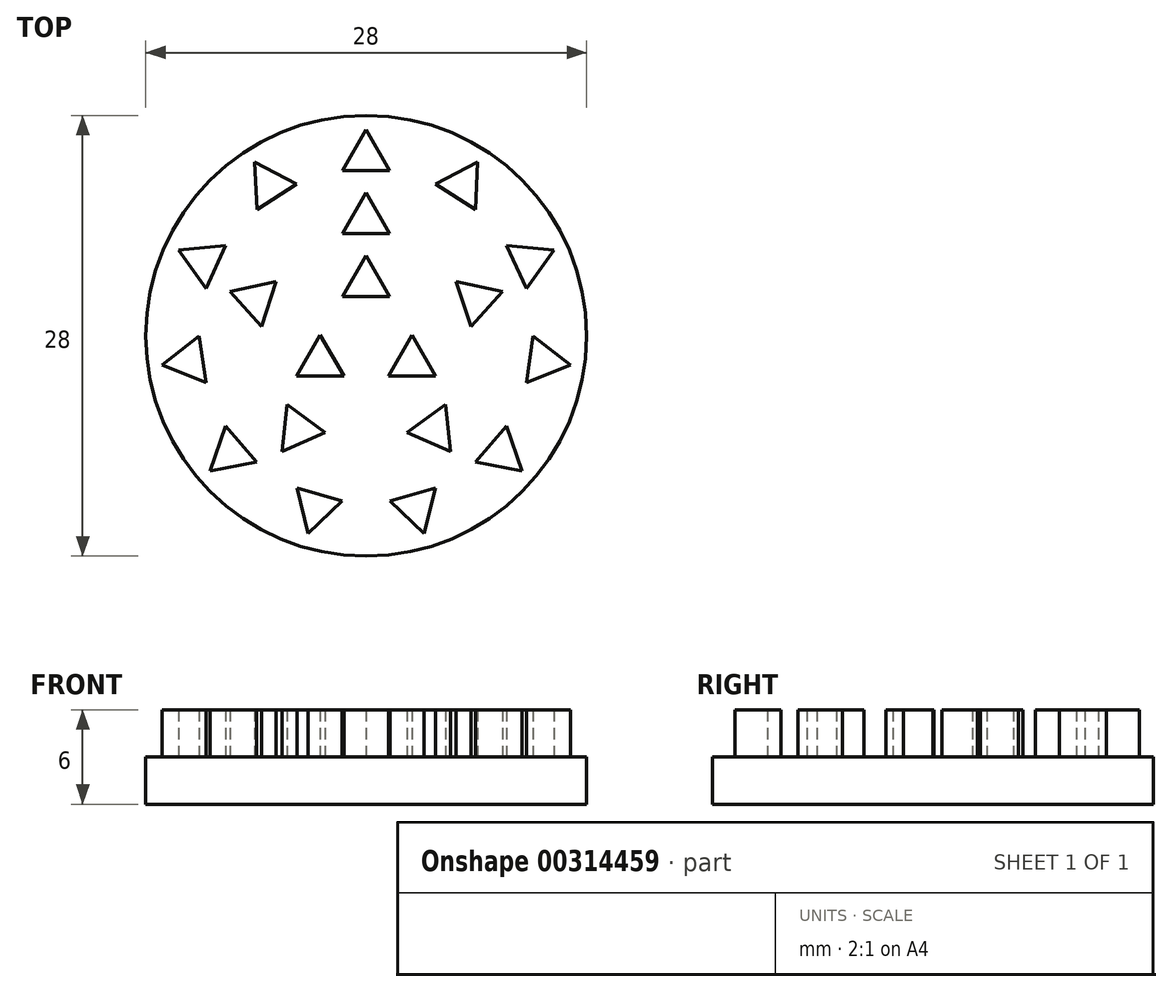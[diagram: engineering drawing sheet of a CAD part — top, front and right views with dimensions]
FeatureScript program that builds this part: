
annotation { "Feature Type Name" : "Feature", "Feature Type Description" : "" }
export const myFeature = defineFeature(function(context is Context, id is Id, definition is map)
    precondition{}
    {
        {
            var Q0;
            Q0=qCreatedBy(makeId("Top.planeOp"),FACE);
            var sketch = newSketch(context, id + "F0", { "sketchPlane" : qUnion([Q0])});
            skCircle(sketch, "E0", {"center": v(0, 0) * mm, "radius": 14 * mm});
            skSolve(sketch);
        }
        {
            var Q0;
            Q0=makeQuery(id+"F0.imprint","IMPRINT",FACE,{"disambiguationData":[TD([[makeQuery(id+"F0.imprint","IMPRINT",EDGE,{"derivedFrom":sQuery(id+"F0.wireOp",EDGE,"E0")}),1.0]])]});
            extrude(context, id + "F1", {"entities" : qUnion([Q0]), "depth" : 3 * mm});
        }
        {
            var Q0;
            Q0=makeQuery(id+"F1.opExtrude","CAP_FACE",FACE,{"disambiguationData":[OSD([sQuery(id+"F0.wireOp",EDGE,"E0")])],"isStart":false});
            var sketch = newSketch(context, id + "F2", { "sketchPlane" : qUnion([Q0])});
            skCircle(sketch, "E1.cCircle", {"center": v(0, 7.37) * mm, "radius": 0.87 * mm, "construction": true});
            skLineSegment(sketch, "E1.0", {"start": v(1.5, 6.5) * mm, "end": v(-1.5, 6.5) * mm});
            skLineSegment(sketch, "E1.1", {"start": v(-1.5, 6.5) * mm, "end": v(0, 9.1) * mm});
            skLineSegment(sketch, "E1.2", {"start": v(0, 9.1) * mm, "end": v(1.5, 6.5) * mm});
            skPoint(sketch, "E1.0.midPoint", {"position": v(0, 6.5) * mm});
            skCircle(sketch, "E2", {"center": v(0, 0) * mm, "radius": 6.5 * mm});
            skLineSegment(sketch, "E3.1.0", {"start": v(-5.72, 3.44) * mm, "end": v(-6.65, 0.58) * mm});
            skLineSegment(sketch, "E3.1.1", {"start": v(-8.65, 2.81) * mm, "end": v(-5.72, 3.44) * mm});
            skLineSegment(sketch, "E3.1.2", {"start": v(-6.65, 0.58) * mm, "end": v(-8.65, 2.81) * mm});
            skCircle(sketch, "E3.1.3", {"center": v(-7, 2.28) * mm, "radius": 0.87 * mm, "construction": true});
            skLineSegment(sketch, "E3.2.0", {"start": v(-5.03, -4.38) * mm, "end": v(-2.6, -6.14) * mm});
            skLineSegment(sketch, "E3.2.1", {"start": v(-5.35, -7.36) * mm, "end": v(-5.03, -4.38) * mm});
            skLineSegment(sketch, "E3.2.2", {"start": v(-2.6, -6.14) * mm, "end": v(-5.35, -7.36) * mm});
            skCircle(sketch, "E3.2.3", {"center": v(-4.33, -5.96) * mm, "radius": 0.87 * mm, "construction": true});
            skCircle(sketch, "E4.cCircle", {"center": v(0, 11.37) * mm, "radius": 0.87 * mm, "construction": true});
            skLineSegment(sketch, "E4.0", {"start": v(1.5, 10.5) * mm, "end": v(-1.5, 10.5) * mm});
            skLineSegment(sketch, "E4.1", {"start": v(-1.5, 10.5) * mm, "end": v(0, 13.1) * mm});
            skLineSegment(sketch, "E4.2", {"start": v(0, 13.1) * mm, "end": v(1.5, 10.5) * mm});
            skPoint(sketch, "E4.0.midPoint", {"position": v(0, 10.5) * mm});
            skCircle(sketch, "E5", {"center": v(0, 0) * mm, "radius": 10.5 * mm});
            skLineSegment(sketch, "E6.1.0", {"start": v(-4.41, 9.64) * mm, "end": v(-6.94, 8.02) * mm});
            skLineSegment(sketch, "E6.1.1", {"start": v(-7.08, 11.02) * mm, "end": v(-4.41, 9.64) * mm});
            skLineSegment(sketch, "E6.1.2", {"start": v(-6.94, 8.02) * mm, "end": v(-7.08, 11.02) * mm});
            skCircle(sketch, "E6.1.3", {"center": v(-6.14, 9.56) * mm, "radius": 0.87 * mm, "construction": true});
            skLineSegment(sketch, "E6.2.0", {"start": v(-8.93, 5.73) * mm, "end": v(-10.17, 3) * mm});
            skLineSegment(sketch, "E6.2.1", {"start": v(-11.91, 5.44) * mm, "end": v(-8.93, 5.73) * mm});
            skLineSegment(sketch, "E6.2.2", {"start": v(-10.17, 3) * mm, "end": v(-11.91, 5.44) * mm});
            skCircle(sketch, "E6.2.3", {"center": v(-10.34, 4.72) * mm, "radius": 0.87 * mm, "construction": true});
            skLineSegment(sketch, "E7.2.3.0", {"start": v(-10.6, 0) * mm, "end": v(-10.18, -2.98) * mm});
            skLineSegment(sketch, "E7.3.3.0", {"start": v(-12.96, -1.86) * mm, "end": v(-10.6, 0) * mm});
            skLineSegment(sketch, "E7.6.3.0", {"start": v(-10.18, -2.98) * mm, "end": v(-12.96, -1.86) * mm});
            skCircle(sketch, "E7.9.3.0", {"center": v(-11.25, -1.62) * mm, "radius": 0.87 * mm, "construction": true});
            skLineSegment(sketch, "E7.2.4.0", {"start": v(-8.92, -5.74) * mm, "end": v(-6.95, -8) * mm});
            skLineSegment(sketch, "E7.3.4.0", {"start": v(-9.9, -8.58) * mm, "end": v(-8.92, -5.74) * mm});
            skLineSegment(sketch, "E7.6.4.0", {"start": v(-6.95, -8) * mm, "end": v(-9.9, -8.58) * mm});
            skCircle(sketch, "E7.9.4.0", {"center": v(-8.59, -7.44) * mm, "radius": 0.87 * mm, "construction": true});
            skLineSegment(sketch, "E7.2.5.0", {"start": v(-4.4, -9.65) * mm, "end": v(-1.52, -10.5) * mm});
            skLineSegment(sketch, "E7.3.5.0", {"start": v(-3.7, -12.57) * mm, "end": v(-4.4, -9.65) * mm});
            skLineSegment(sketch, "E7.6.5.0", {"start": v(-1.52, -10.5) * mm, "end": v(-3.7, -12.57) * mm});
            skCircle(sketch, "E7.9.5.0", {"center": v(-3.2, -10.9) * mm, "radius": 0.87 * mm, "construction": true});
            skLineSegment(sketch, "E7.2.6.0", {"start": v(1.52, -10.5) * mm, "end": v(4.4, -9.65) * mm});
            skLineSegment(sketch, "E7.3.6.0", {"start": v(3.7, -12.57) * mm, "end": v(1.52, -10.5) * mm});
            skLineSegment(sketch, "E7.6.6.0", {"start": v(4.4, -9.65) * mm, "end": v(3.7, -12.57) * mm});
            skCircle(sketch, "E7.9.6.0", {"center": v(3.2, -10.9) * mm, "radius": 0.87 * mm, "construction": true});
            skPoint(sketch, "E8", {"position": v(5.68, 8.83) * mm});
            skPoint(sketch, "E9", {"position": v(-2.96, -10.07) * mm});
            skPoint(sketch, "E10", {"position": v(-7.94, -6.88) * mm});
            skPoint(sketch, "E11", {"position": v(-10.4, -1.5) * mm});
            skPoint(sketch, "E12", {"position": v(-9.55, 4.36) * mm});
            skPoint(sketch, "E13", {"position": v(-5.68, 8.83) * mm});
            skPoint(sketch, "E14", {"position": v(6.18, 2) * mm});
            skPoint(sketch, "E15", {"position": v(-6.18, 2) * mm});
            skLineSegment(sketch, "E16.2.7.0", {"start": v(6.95, -8) * mm, "end": v(8.92, -5.74) * mm});
            skLineSegment(sketch, "E16.3.7.0", {"start": v(9.9, -8.58) * mm, "end": v(6.95, -8) * mm});
            skLineSegment(sketch, "E16.6.7.0", {"start": v(8.92, -5.74) * mm, "end": v(9.9, -8.58) * mm});
            skCircle(sketch, "E16.9.7.0", {"center": v(8.59, -7.44) * mm, "radius": 0.87 * mm, "construction": true});
            skLineSegment(sketch, "E16.2.8.0", {"start": v(10.18, -2.98) * mm, "end": v(10.6, 0) * mm});
            skLineSegment(sketch, "E16.3.8.0", {"start": v(12.96, -1.86) * mm, "end": v(10.18, -2.98) * mm});
            skLineSegment(sketch, "E16.6.8.0", {"start": v(10.6, 0) * mm, "end": v(12.96, -1.86) * mm});
            skCircle(sketch, "E16.9.8.0", {"center": v(11.25, -1.62) * mm, "radius": 0.87 * mm, "construction": true});
            skLineSegment(sketch, "E16.2.9.0", {"start": v(10.17, 3) * mm, "end": v(8.93, 5.73) * mm});
            skLineSegment(sketch, "E16.3.9.0", {"start": v(11.91, 5.44) * mm, "end": v(10.17, 3) * mm});
            skLineSegment(sketch, "E16.6.9.0", {"start": v(8.93, 5.73) * mm, "end": v(11.91, 5.44) * mm});
            skCircle(sketch, "E16.9.9.0", {"center": v(10.34, 4.72) * mm, "radius": 0.87 * mm, "construction": true});
            skCircle(sketch, "E17.cCircle", {"center": v(0, 3.37) * mm, "radius": 0.87 * mm, "construction": true});
            skLineSegment(sketch, "E17.0", {"start": v(1.5, 2.5) * mm, "end": v(-1.5, 2.5) * mm});
            skLineSegment(sketch, "E17.1", {"start": v(-1.5, 2.5) * mm, "end": v(0, 5.1) * mm});
            skLineSegment(sketch, "E17.2", {"start": v(0, 5.1) * mm, "end": v(1.5, 2.5) * mm});
            skPoint(sketch, "E17.0.midPoint", {"position": v(0, 2.5) * mm});
            skCircle(sketch, "E18", {"center": v(0, 0) * mm, "radius": 2.5 * mm});
            skLineSegment(sketch, "E19.1.0", {"start": v(-2.92, 0.05) * mm, "end": v(-1.42, -2.55) * mm});
            skLineSegment(sketch, "E19.1.1", {"start": v(-4.42, -2.55) * mm, "end": v(-2.92, 0.05) * mm});
            skLineSegment(sketch, "E19.1.2", {"start": v(-1.42, -2.55) * mm, "end": v(-4.42, -2.55) * mm});
            skCircle(sketch, "E19.1.3", {"center": v(-2.92, -1.68) * mm, "radius": 0.87 * mm, "construction": true});
            skLineSegment(sketch, "E19.2.0", {"start": v(1.42, -2.55) * mm, "end": v(2.92, 0.05) * mm});
            skLineSegment(sketch, "E19.2.1", {"start": v(4.42, -2.55) * mm, "end": v(1.42, -2.55) * mm});
            skLineSegment(sketch, "E19.2.2", {"start": v(2.92, 0.05) * mm, "end": v(4.42, -2.55) * mm});
            skCircle(sketch, "E19.2.3", {"center": v(2.92, -1.68) * mm, "radius": 0.87 * mm, "construction": true});
            skPoint(sketch, "E20", {"position": v(2.17, -1.25) * mm});
            skPoint(sketch, "E21", {"position": v(-2.17, -1.25) * mm});
            skLineSegment(sketch, "E22.2.3.0", {"start": v(2.6, -6.14) * mm, "end": v(5.03, -4.38) * mm});
            skLineSegment(sketch, "E22.3.3.0", {"start": v(5.35, -7.36) * mm, "end": v(2.6, -6.14) * mm});
            skLineSegment(sketch, "E22.6.3.0", {"start": v(5.03, -4.38) * mm, "end": v(5.35, -7.36) * mm});
            skCircle(sketch, "E22.9.3.0", {"center": v(4.33, -5.96) * mm, "radius": 0.87 * mm, "construction": true});
            skLineSegment(sketch, "E22.2.4.0", {"start": v(6.65, 0.58) * mm, "end": v(5.72, 3.44) * mm});
            skLineSegment(sketch, "E22.3.4.0", {"start": v(8.65, 2.81) * mm, "end": v(6.65, 0.58) * mm});
            skLineSegment(sketch, "E22.6.4.0", {"start": v(5.72, 3.44) * mm, "end": v(8.65, 2.81) * mm});
            skCircle(sketch, "E22.9.4.0", {"center": v(7, 2.28) * mm, "radius": 0.87 * mm, "construction": true});
            skLineSegment(sketch, "E23.2.10.0", {"start": v(6.94, 8.02) * mm, "end": v(4.41, 9.64) * mm});
            skLineSegment(sketch, "E23.3.10.0", {"start": v(7.08, 11.02) * mm, "end": v(6.94, 8.02) * mm});
            skLineSegment(sketch, "E23.6.10.0", {"start": v(4.41, 9.64) * mm, "end": v(7.08, 11.02) * mm});
            skCircle(sketch, "E23.9.10.0", {"center": v(6.14, 9.56) * mm, "radius": 0.87 * mm, "construction": true});
            skSolve(sketch);
        }
        {
            var Q0;
            {var subQ3=sQuery(id+"F2.wireOp",EDGE,"8b3eb6cf-7dbc-4c96-a035-3d80c259cfac.1");Q0=makeQuery(id+"F2.imprint","IMPRINT",FACE,{"disambiguationData":[TD([[makeQuery(id+"F2.imprint","IMPRINT",EDGE,{"derivedFrom":subQ3}),-1.0]])]});}
            var Q1;
            {var subQ0=sQuery(id+"F2.wireOp",EDGE,"6c10d993-edd7-4a8d-bda8-a9486d968e1a.5.1");Q1=makeQuery(id+"F2.imprint","IMPRINT",FACE,{"disambiguationData":[TD([[makeQuery(id+"F2.imprint","IMPRINT",EDGE,{"derivedFrom":subQ0}),-1.0]])]});}
            var Q2;
            {var subQ0=sQuery(id+"F2.wireOp",EDGE,"6c10d993-edd7-4a8d-bda8-a9486d968e1a.4.1");Q2=makeQuery(id+"F2.imprint","IMPRINT",FACE,{"disambiguationData":[TD([[makeQuery(id+"F2.imprint","IMPRINT",EDGE,{"derivedFrom":subQ0}),-1.0]])]});}
            var Q3;
            {var subQ0=sQuery(id+"F2.wireOp",EDGE,"6c10d993-edd7-4a8d-bda8-a9486d968e1a.3.1");Q3=makeQuery(id+"F2.imprint","IMPRINT",FACE,{"disambiguationData":[TD([[makeQuery(id+"F2.imprint","IMPRINT",EDGE,{"derivedFrom":subQ0}),-1.0]])]});}
            var Q4;
            {var subQ0=sQuery(id+"F2.wireOp",EDGE,"6c10d993-edd7-4a8d-bda8-a9486d968e1a.2.1");Q4=makeQuery(id+"F2.imprint","IMPRINT",FACE,{"disambiguationData":[TD([[makeQuery(id+"F2.imprint","IMPRINT",EDGE,{"derivedFrom":subQ0}),-1.0]])]});}
            var Q5;
            {var subQ0=sQuery(id+"F2.wireOp",EDGE,"6c10d993-edd7-4a8d-bda8-a9486d968e1a.1.1");Q5=makeQuery(id+"F2.imprint","IMPRINT",FACE,{"disambiguationData":[TD([[makeQuery(id+"F2.imprint","IMPRINT",EDGE,{"derivedFrom":subQ0}),-1.0]])]});}
            var Q6;
            {var subQ0=sQuery(id+"F2.wireOp",EDGE,"947e9cf8-dde9-4160-9a07-f35e782527b7.3.7.0");Q6=makeQuery(id+"F2.imprint","IMPRINT",FACE,{"disambiguationData":[TD([[makeQuery(id+"F2.imprint","IMPRINT",EDGE,{"derivedFrom":subQ0}),-1.0]])]});}
            var Q7;
            {var subQ0=sQuery(id+"F2.wireOp",EDGE,"947e9cf8-dde9-4160-9a07-f35e782527b7.3.6.0");Q7=makeQuery(id+"F2.imprint","IMPRINT",FACE,{"disambiguationData":[TD([[makeQuery(id+"F2.imprint","IMPRINT",EDGE,{"derivedFrom":subQ0}),-1.0]])]});}
            var Q8;
            {var subQ0=sQuery(id+"F2.wireOp",EDGE,"947e9cf8-dde9-4160-9a07-f35e782527b7.11.7.0");Q8=makeQuery(id+"F2.imprint","IMPRINT",FACE,{"disambiguationData":[TD([[makeQuery(id+"F2.imprint","IMPRINT",EDGE,{"derivedFrom":subQ0}),-1.0]])]});}
            var Q9;
            {var subQ0=sQuery(id+"F2.wireOp",EDGE,"E1.1");Q9=makeQuery(id+"F2.imprint","IMPRINT",FACE,{"disambiguationData":[TD([[makeQuery(id+"F2.imprint","IMPRINT",EDGE,{"derivedFrom":subQ0}),-1.0]])]});}
            var Q10;
            {var subQ0=sQuery(id+"F2.wireOp",EDGE,"E1.2");Q10=makeQuery(id+"F2.imprint","IMPRINT",FACE,{"disambiguationData":[TD([[makeQuery(id+"F2.imprint","IMPRINT",EDGE,{"derivedFrom":subQ0}),-1.0]])]});}
            var Q11;
            {var subQ0=sQuery(id+"F2.wireOp",EDGE,"E3.1.1");Q11=makeQuery(id+"F2.imprint","IMPRINT",FACE,{"disambiguationData":[TD([[makeQuery(id+"F2.imprint","IMPRINT",EDGE,{"derivedFrom":subQ0}),-1.0]])]});}
            var Q12;
            {var subQ0=sQuery(id+"F2.wireOp",EDGE,"E3.2.1");Q12=makeQuery(id+"F2.imprint","IMPRINT",FACE,{"disambiguationData":[TD([[makeQuery(id+"F2.imprint","IMPRINT",EDGE,{"derivedFrom":subQ0}),-1.0]])]});}
            var Q13;
            {var subQ0=sQuery(id+"F2.wireOp",EDGE,"78a639ae-5dbe-4d62-8846-17a8c4bbea7f.3.3.0");Q13=makeQuery(id+"F2.imprint","IMPRINT",FACE,{"disambiguationData":[TD([[makeQuery(id+"F2.imprint","IMPRINT",EDGE,{"derivedFrom":subQ0}),-1.0]])]});}
            var Q14;
            {var subQ0=sQuery(id+"F2.wireOp",EDGE,"E6.1.1");Q14=makeQuery(id+"F2.imprint","IMPRINT",FACE,{"disambiguationData":[TD([[makeQuery(id+"F2.imprint","IMPRINT",EDGE,{"derivedFrom":subQ0}),-1.0]])]});}
            var Q15;
            {var subQ3=sQuery(id+"F2.wireOp",EDGE,"E4.1");Q15=makeQuery(id+"F2.imprint","IMPRINT",FACE,{"disambiguationData":[TD([[makeQuery(id+"F2.imprint","IMPRINT",EDGE,{"derivedFrom":subQ3}),-1.0]])]});}
            var Q16;
            {var subQ0=sQuery(id+"F2.wireOp",EDGE,"E7.3.7.0");Q16=makeQuery(id+"F2.imprint","IMPRINT",FACE,{"disambiguationData":[TD([[makeQuery(id+"F2.imprint","IMPRINT",EDGE,{"derivedFrom":subQ0}),-1.0]])]});}
            var Q17;
            {var subQ0=sQuery(id+"F2.wireOp",EDGE,"E7.3.6.0");Q17=makeQuery(id+"F2.imprint","IMPRINT",FACE,{"disambiguationData":[TD([[makeQuery(id+"F2.imprint","IMPRINT",EDGE,{"derivedFrom":subQ0}),-1.0]])]});}
            var Q18;
            {var subQ0=sQuery(id+"F2.wireOp",EDGE,"E7.3.5.0");Q18=makeQuery(id+"F2.imprint","IMPRINT",FACE,{"disambiguationData":[TD([[makeQuery(id+"F2.imprint","IMPRINT",EDGE,{"derivedFrom":subQ0}),-1.0]])]});}
            var Q19;
            {var subQ0=sQuery(id+"F2.wireOp",EDGE,"E7.3.4.0");Q19=makeQuery(id+"F2.imprint","IMPRINT",FACE,{"disambiguationData":[TD([[makeQuery(id+"F2.imprint","IMPRINT",EDGE,{"derivedFrom":subQ0}),-1.0]])]});}
            var Q20;
            {var subQ0=sQuery(id+"F2.wireOp",EDGE,"E7.3.3.0");Q20=makeQuery(id+"F2.imprint","IMPRINT",FACE,{"disambiguationData":[TD([[makeQuery(id+"F2.imprint","IMPRINT",EDGE,{"derivedFrom":subQ0}),-1.0]])]});}
            var Q21;
            {var subQ0=sQuery(id+"F2.wireOp",EDGE,"E16.3.14.0");Q21=makeQuery(id+"F2.imprint","IMPRINT",FACE,{"disambiguationData":[TD([[makeQuery(id+"F2.imprint","IMPRINT",EDGE,{"derivedFrom":subQ0}),-1.0]])]});}
            var Q22;
            {var subQ0=sQuery(id+"F2.wireOp",EDGE,"E22.3.6.0");Q22=makeQuery(id+"F2.imprint","IMPRINT",FACE,{"disambiguationData":[TD([[makeQuery(id+"F2.imprint","IMPRINT",EDGE,{"derivedFrom":subQ0}),-1.0]])]});}
            var Q23;
            {var subQ0=sQuery(id+"F2.wireOp",EDGE,"E16.3.13.0");Q23=makeQuery(id+"F2.imprint","IMPRINT",FACE,{"disambiguationData":[TD([[makeQuery(id+"F2.imprint","IMPRINT",EDGE,{"derivedFrom":subQ0}),-1.0]])]});}
            var Q24;
            {var subQ0=sQuery(id+"F2.wireOp",EDGE,"E16.3.12.0");Q24=makeQuery(id+"F2.imprint","IMPRINT",FACE,{"disambiguationData":[TD([[makeQuery(id+"F2.imprint","IMPRINT",EDGE,{"derivedFrom":subQ0}),-1.0]])]});}
            var Q25;
            {var subQ3=sQuery(id+"F2.wireOp",EDGE,"E17.1");Q25=makeQuery(id+"F2.imprint","IMPRINT",FACE,{"disambiguationData":[TD([[makeQuery(id+"F2.imprint","IMPRINT",EDGE,{"derivedFrom":subQ3}),-1.0]])]});}
            var Q26;
            {var subQ0=sQuery(id+"F2.wireOp",EDGE,"E19.1.1");Q26=makeQuery(id+"F2.imprint","IMPRINT",FACE,{"disambiguationData":[TD([[makeQuery(id+"F2.imprint","IMPRINT",EDGE,{"derivedFrom":subQ0}),-1.0]])]});}
            var Q27;
            {var subQ0=sQuery(id+"F2.wireOp",EDGE,"E19.2.1");Q27=makeQuery(id+"F2.imprint","IMPRINT",FACE,{"disambiguationData":[TD([[makeQuery(id+"F2.imprint","IMPRINT",EDGE,{"derivedFrom":subQ0}),-1.0]])]});}
            var Q28;
            {var subQ0=sQuery(id+"F2.wireOp",EDGE,"E22.3.5.0");Q28=makeQuery(id+"F2.imprint","IMPRINT",FACE,{"disambiguationData":[TD([[makeQuery(id+"F2.imprint","IMPRINT",EDGE,{"derivedFrom":subQ0}),-1.0]])]});}
            var Q29;
            {var subQ0=sQuery(id+"F2.wireOp",EDGE,"E16.3.11.0");Q29=makeQuery(id+"F2.imprint","IMPRINT",FACE,{"disambiguationData":[TD([[makeQuery(id+"F2.imprint","IMPRINT",EDGE,{"derivedFrom":subQ0}),-1.0]])]});}
            var Q30;
            {var subQ0=sQuery(id+"F2.wireOp",EDGE,"E16.3.10.0");Q30=makeQuery(id+"F2.imprint","IMPRINT",FACE,{"disambiguationData":[TD([[makeQuery(id+"F2.imprint","IMPRINT",EDGE,{"derivedFrom":subQ0}),-1.0]])]});}
            var Q31;
            {var subQ0=sQuery(id+"F2.wireOp",EDGE,"E16.3.9.0");Q31=makeQuery(id+"F2.imprint","IMPRINT",FACE,{"disambiguationData":[TD([[makeQuery(id+"F2.imprint","IMPRINT",EDGE,{"derivedFrom":subQ0}),-1.0]])]});}
            var Q32;
            {var subQ0=sQuery(id+"F2.wireOp",EDGE,"E22.3.4.0");Q32=makeQuery(id+"F2.imprint","IMPRINT",FACE,{"disambiguationData":[TD([[makeQuery(id+"F2.imprint","IMPRINT",EDGE,{"derivedFrom":subQ0}),-1.0]])]});}
            var Q33;
            {var subQ0=sQuery(id+"F2.wireOp",EDGE,"E22.3.3.0");Q33=makeQuery(id+"F2.imprint","IMPRINT",FACE,{"disambiguationData":[TD([[makeQuery(id+"F2.imprint","IMPRINT",EDGE,{"derivedFrom":subQ0}),-1.0]])]});}
            var Q34;
            {var subQ0=sQuery(id+"F2.wireOp",EDGE,"E16.3.7.0");Q34=makeQuery(id+"F2.imprint","IMPRINT",FACE,{"disambiguationData":[TD([[makeQuery(id+"F2.imprint","IMPRINT",EDGE,{"derivedFrom":subQ0}),-1.0]])]});}
            var Q35;
            {var subQ0=sQuery(id+"F2.wireOp",EDGE,"E16.3.8.0");Q35=makeQuery(id+"F2.imprint","IMPRINT",FACE,{"disambiguationData":[TD([[makeQuery(id+"F2.imprint","IMPRINT",EDGE,{"derivedFrom":subQ0}),-1.0]])]});}
            var Q36;
            {var subQ0=sQuery(id+"F2.wireOp",EDGE,"E6.2.1");Q36=makeQuery(id+"F2.imprint","IMPRINT",FACE,{"disambiguationData":[TD([[makeQuery(id+"F2.imprint","IMPRINT",EDGE,{"derivedFrom":subQ0}),-1.0]])]});}
            var Q37;
            {var subQ0=sQuery(id+"F2.wireOp",EDGE,"272dc005-faef-4720-9c03-485c8fccf4ae.3.3.0");Q37=makeQuery(id+"F2.imprint","IMPRINT",FACE,{"disambiguationData":[TD([[makeQuery(id+"F2.imprint","IMPRINT",EDGE,{"derivedFrom":subQ0}),-1.0]])]});}
            var Q38;
            {var subQ0=sQuery(id+"F2.wireOp",EDGE,"928bc74c-74d0-45c7-9305-7819a02c8b73.3.7.0");Q38=makeQuery(id+"F2.imprint","IMPRINT",FACE,{"disambiguationData":[TD([[makeQuery(id+"F2.imprint","IMPRINT",EDGE,{"derivedFrom":subQ0}),-1.0]])]});}
            var Q39;
            {var subQ0=sQuery(id+"F2.wireOp",EDGE,"ea4922ad-3ce4-4be6-aee5-9cdb8b6c6196.3.15.0");Q39=makeQuery(id+"F2.imprint","IMPRINT",FACE,{"disambiguationData":[TD([[makeQuery(id+"F2.imprint","IMPRINT",EDGE,{"derivedFrom":subQ0}),-1.0]])]});}
            var Q40;
            {var subQ0=sQuery(id+"F2.wireOp",EDGE,"E23.3.10.0");Q40=makeQuery(id+"F2.imprint","IMPRINT",FACE,{"disambiguationData":[TD([[makeQuery(id+"F2.imprint","IMPRINT",EDGE,{"derivedFrom":subQ0}),-1.0]])]});}
            extrude(context, id + "F3", {"entities" : qUnion([Q0, Q1, Q2, Q3, Q4, Q5, Q6, Q7, Q8, Q9, Q10, Q11, Q12, Q13, Q14, Q15, Q16, Q17, Q18, Q19, Q20, Q21, Q22, Q23, Q24, Q25, Q26, Q27, Q28, Q29, Q30, Q31, Q32, Q33, Q34, Q35, Q36, Q37, Q38, Q39, Q40]), "operationType" : NewBodyOperationType.ADD, "depth" : 3 * mm});
        }
    });
